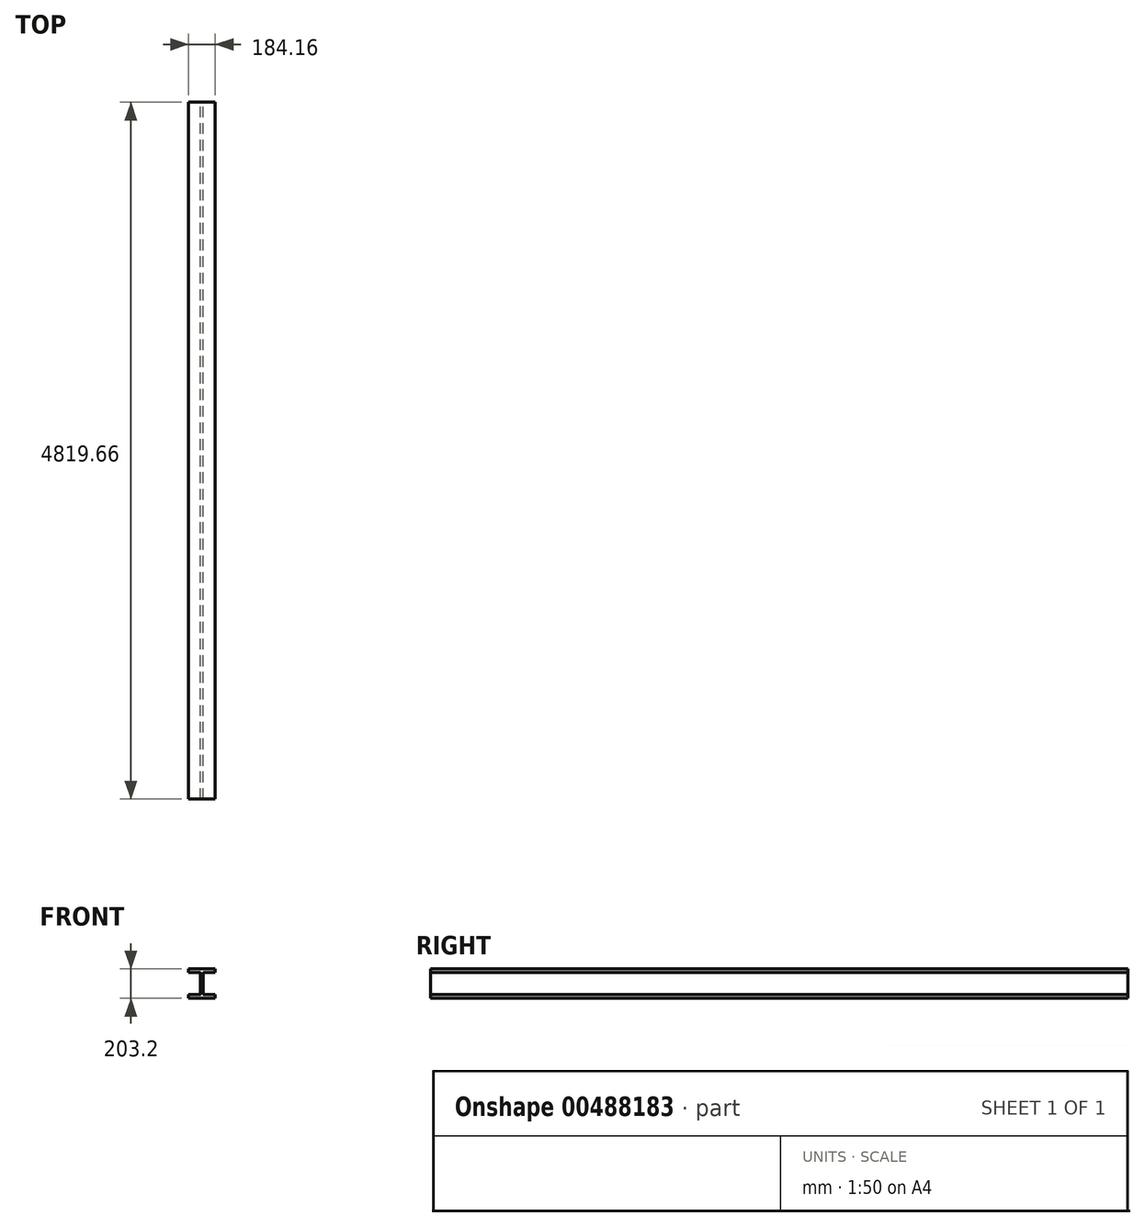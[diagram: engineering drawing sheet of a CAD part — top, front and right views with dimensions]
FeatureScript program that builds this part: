
annotation { "Feature Type Name" : "Feature", "Feature Type Description" : "" }
export const myFeature = defineFeature(function(context is Context, id is Id, definition is map)
    precondition{}
    {
        {
            var Q0;
            Q0=qCreatedBy(makeId("Front.planeOp"),FACE);
            var sketch = newSketch(context, id + "F0", { "sketchPlane" : qUnion([Q0])});
            skLineSegment(sketch, "E0", {"start": v(92.08, -76.2) * mm, "end": v(12.07, -76.2) * mm});
            skLineSegment(sketch, "E1", {"start": v(9.52, -73.66) * mm, "end": v(9.52, 73.66) * mm});
            skLineSegment(sketch, "E2", {"start": v(12.07, 76.2) * mm, "end": v(92.08, 76.2) * mm});
            skLineSegment(sketch, "E3", {"start": v(-92.08, 76.2) * mm, "end": v(-12.07, 76.2) * mm});
            skLineSegment(sketch, "E4", {"start": v(-9.53, 73.66) * mm, "end": v(-9.53, -73.66) * mm});
            skLineSegment(sketch, "E5", {"start": v(-12.06, -76.2) * mm, "end": v(-92.08, -76.2) * mm});
            skLineSegment(sketch, "E6", {"start": v(0, 0) * mm, "end": v(-9.52, 0) * mm, "construction": true});
            skLineSegment(sketch, "E7", {"start": v(0, 0) * mm, "end": v(9.52, 0) * mm, "construction": true});
            skLineSegment(sketch, "E8", {"start": v(0, 0) * mm, "end": v(0, 101.6) * mm, "construction": true});
            skLineSegment(sketch, "E9", {"start": v(0, 0) * mm, "end": v(0, -101.6) * mm, "construction": true});
            skPoint(sketch, "E10.visualSharp", {"position": v(-9.53, 76.2) * mm});
            skArc(sketch, "E10.filletArc", {"start": v(-9.52, 73.66) * mm, "mid": v(-10.27, 75.46) * mm, "end": v(-12.07, 76.2) * mm});
            skPoint(sketch, "E11.visualSharp", {"position": v(9.53, 76.2) * mm});
            skArc(sketch, "E11.filletArc", {"start": v(12.07, 76.2) * mm, "mid": v(10.27, 75.46) * mm, "end": v(9.52, 73.66) * mm});
            skPoint(sketch, "E12.visualSharp", {"position": v(9.53, -76.2) * mm});
            skArc(sketch, "E12.filletArc", {"start": v(9.52, -73.66) * mm, "mid": v(10.27, -75.46) * mm, "end": v(12.07, -76.2) * mm});
            skPoint(sketch, "E13.visualSharp", {"position": v(-9.53, -76.2) * mm});
            skArc(sketch, "E13.filletArc", {"start": v(-12.06, -76.2) * mm, "mid": v(-10.27, -75.46) * mm, "end": v(-9.52, -73.66) * mm});
            skPoint(sketch, "E14.visualSharp", {"position": v(-92.08, 101.6) * mm});
            skPoint(sketch, "E15.visualSharp", {"position": v(92.08, 101.6) * mm});
            skPoint(sketch, "E16.visualSharp", {"position": v(92.08, 76.2) * mm});
            skPoint(sketch, "E17.visualSharp", {"position": v(92.08, -101.6) * mm});
            skPoint(sketch, "E18.visualSharp", {"position": v(-92.08, -76.2) * mm});
            skPoint(sketch, "E19.visualSharp", {"position": v(-92.08, -101.6) * mm});
            skLineSegment(sketch, "E20", {"start": v(92.08, -76.2) * mm, "end": v(92.08, -101.6) * mm});
            skLineSegment(sketch, "E21", {"start": v(-92.08, -76.2) * mm, "end": v(-92.08, -101.6) * mm});
            skLineSegment(sketch, "E22", {"start": v(-92.08, 101.6) * mm, "end": v(-92.08, 76.2) * mm});
            skLineSegment(sketch, "E23", {"start": v(92.08, 101.6) * mm, "end": v(92.08, 76.2) * mm});
            skLineSegment(sketch, "E24", {"start": v(-92.08, 101.6) * mm, "end": v(92.08, 101.6) * mm});
            skLineSegment(sketch, "E25", {"start": v(-92.07, -101.6) * mm, "end": v(92.08, -101.6) * mm});
            skSolve(sketch);
        }
        {
            var Q0;
            Q0=makeQuery(id+"F0.imprint","IMPRINT",FACE,{"disambiguationData":[TD([[makeQuery(id+"F0.imprint","IMPRINT",EDGE,{"derivedFrom":sQuery(id+"F0.wireOp",EDGE,"E0")}),1.0]])]});
            extrude(context, id + "F1", {"entities" : qUnion([Q0]), "endBound" : BoundingType.SYMMETRIC, "depth" : 4572 * mm + 247.65 * mm, "offsetDistance" : 25.4 * mm});
        }
    });
